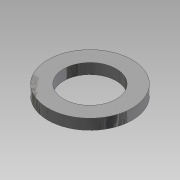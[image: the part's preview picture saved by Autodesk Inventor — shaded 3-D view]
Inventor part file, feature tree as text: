
AUTODESK INVENTOR PART (.ipt)
format: ipt  version: 2013 SP2 (Build 170200200, 200)  size: 77,824 bytes
history: native  units: mm
features: extrude x1, sketch x1
ambient origin geometry x8: Origin, YZ Plane, XZ Plane, XY Plane, X Axis, Y Axis, Z Axis, Center Point
bodies: Solid1 (feature_tree)
feature tree (2):
  extrude  "Extrusion1"  Depth=8.0mm
  sketch  "Sketch1"  dims[d0=5.0mm d1=8.0mm d2=1.0mm d3=0.0mm]
